# Revit family: Light_Fixture-Wall_Sconce-KOHLER-Bellera-K-38406
name_source: partatom
category: Lighting Fixtures
units: mm (PartAtom-declared; Revit-internal decimal feet)

## family parameters
Cut with Voids When Loaded = No
Host = Face
Light Source = Yes
OmniClass Number = 23.35.47.11
OmniClass Title = Lighting Fixtures
Part Type = Normal
Room Calculation Point = No
Round Connector Dimension = Use Diameter
Shared = No

## types (5) — shared parameters
ADA Compliant = No
Apparent Load = 0 VA
Assembly Code = D5040.50
Color Filter = 16777215
Date Modified = 08/30/2023
Default Elevation = 60"
Description = Frosted Three Light Scone
Dimming Lamp Color Temperature Shift = Incandescent Lamp Curve
Electrical Connector = Yes
Electrical Note = One Dedicated Circuit Required
Hardware Included = No
Height = 5 15/16"
Lamp = 3*E26 BULB
Length = 24 3/4"
Light Source Symbol Size = 2"
Manufacturer = Kohler Co.
Master Format 2014 = 26 51 13
Master Format 2014 Name = Interior Lighting Fixtures, Lamps, And Ballasts
Material = Premium Metal Construction
Product Documentation Link = https://www.us.kohler.com
Product Name = Bellera
Product Page URL = http://www.us.kohler.com
URL = https://www.us.kohler.com
Voltage = 120 V
WaterSense Certified = No
Wattage Comments = Max 60W*3 BULB
Width = 8 3/4"

## per-type parameters (varying)
| type | Finish | Model | Type |
| CPL-Polished Chrome | KOHLER-Metal-CPL-Polished_Chrome | K-38406-SC03-CPL | 5 |
| 2GL-Brushed Modern Brass | KOHLER-Metal-2GL-Brushed_Modern_Brass | K-38406-SC03-2GL | 1 |
| BNL-Brushed Nickel | KOHLER-Metal-BNL-Brushed_Nickel | K-38406-SC03-BNL | 3 |
| BLL-Matte Black | KOHLER-Metal-BLL-Matte_Black | K-38406-SC03-BLL | 2 |
| BZL-Oil Rubbed Bronze | KOHLER-Metal-BZL-Oil_Rubbed_Bronze | K-38406-SC03-BZL | 4 |

## geometry (parser evidence)
native form markers: Sweep x8
no freeform markers — native parametric forms only
